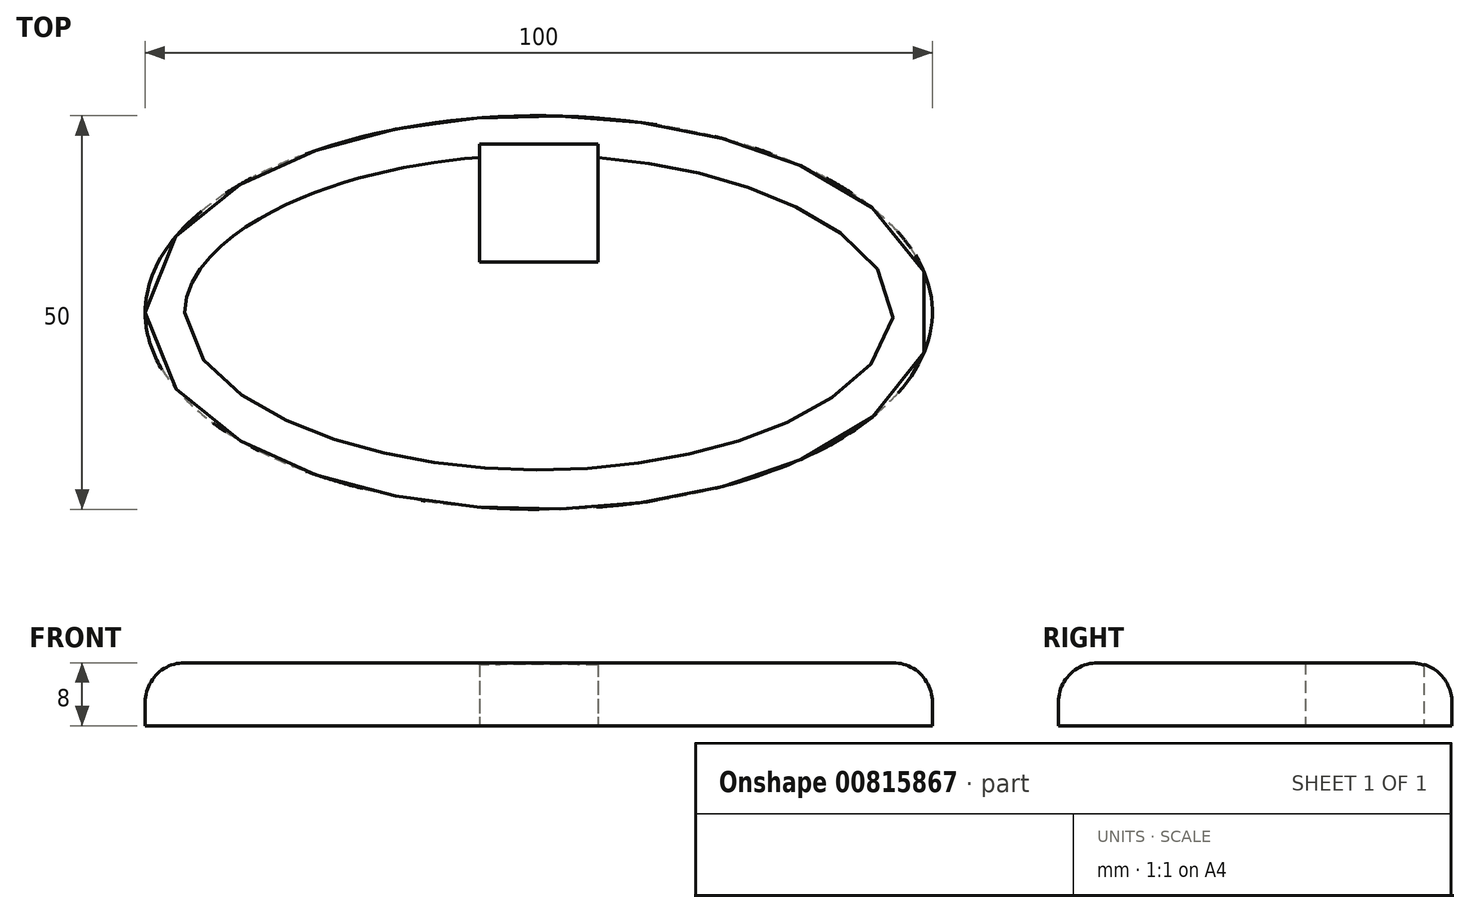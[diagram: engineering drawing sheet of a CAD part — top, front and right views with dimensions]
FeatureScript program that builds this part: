
annotation { "Feature Type Name" : "Feature", "Feature Type Description" : "" }
export const myFeature = defineFeature(function(context is Context, id is Id, definition is map)
    precondition{}
    {
        {
            var Q0;
            Q0=qCreatedBy(makeId("Top.planeOp"),FACE);
            var sketch = newSketch(context, id + "F0", { "sketchPlane" : qUnion([Q0])});
            skEllipse(sketch, "E0", {"center": v(0, 0) * mm, "majorRadius": 50 * mm, "minorRadius": 25 * mm, "majorAxis": v(-1, 0)});
            skLineSegment(sketch, "E1.bottom", {"start": v(-7.5, 21.4) * mm, "end": v(7.5, 21.4) * mm});
            skLineSegment(sketch, "E1.top", {"start": v(-7.5, 6.4) * mm, "end": v(7.5, 6.4) * mm});
            skLineSegment(sketch, "E1.left", {"start": v(-7.5, 21.4) * mm, "end": v(-7.5, 6.4) * mm});
            skLineSegment(sketch, "E1.right", {"start": v(7.5, 21.4) * mm, "end": v(7.5, 6.4) * mm});
            skPoint(sketch, "E1.middle", {"position": v(0, 13.9) * mm});
            skSolve(sketch);
        }
        {
            var Q0;
            Q0 = qSketchRegion(id + "F0", true);
            extrude(context, id + "F1", {"entities" : qUnion([Q0]), "depth" : 8 * mm, "offsetDistance" : 25 * mm});
        }
        {
            var Q0;
            Q0=makeQuery(id+"F1.opExtrude","CAP_EDGE",EDGE,{"disambiguationData":[OSD([sQuery(id+"F0.wireOp",EDGE,"E0")])],"isStart":false});
            fillet(context, id + "F2", {"entities" : qUnion([Q0]), "radius" : 5 * mm, "tangentPropagation" : true, "allowEdgeOverflow" : false});
        }
        {
            var Q0;
            Q0=makeQuery(id+"F0.imprint","IMPRINT",FACE,{"disambiguationData":[TD([[makeQuery(id+"F0.imprint","IMPRINT",EDGE,{"derivedFrom":sQuery(id+"F0.wireOp",EDGE,"E1.bottom")}),-1.0]])]});
            extrude(context, id + "F3", {"entities" : qUnion([Q0]), "operationType" : NewBodyOperationType.REMOVE, "oppositeDirection" : true, "depth" : 25 * mm, "offsetDistance" : 25 * mm});
        }
    });
